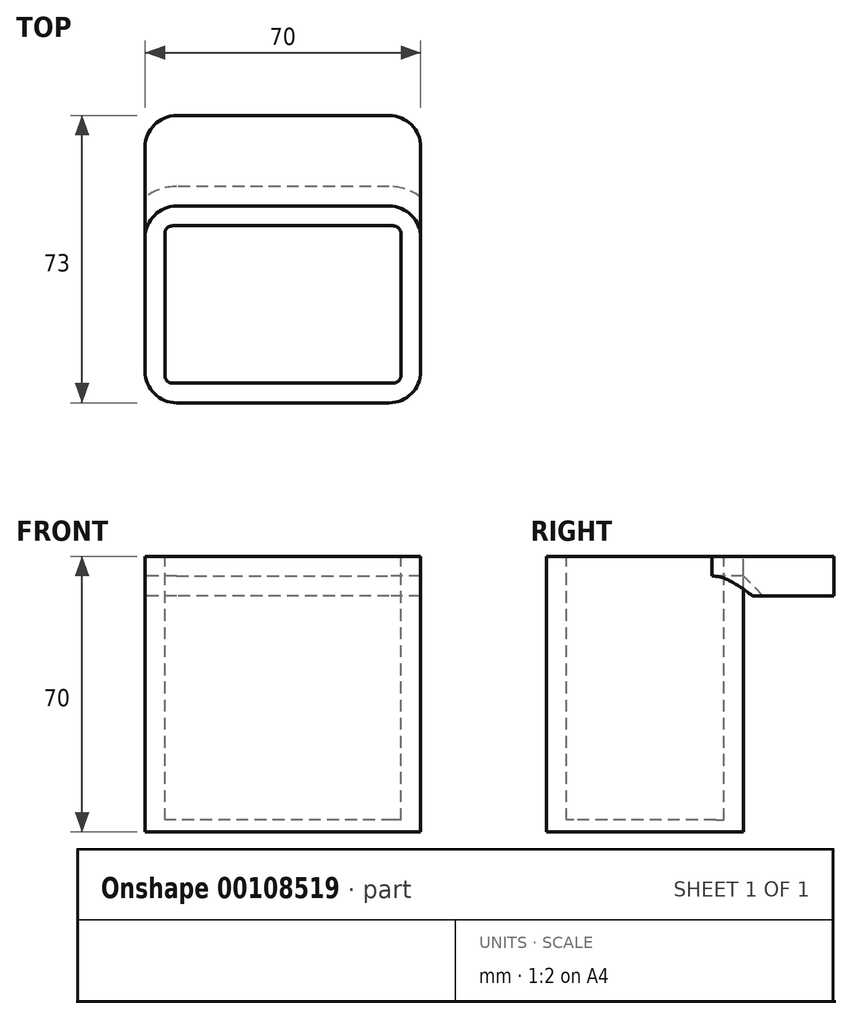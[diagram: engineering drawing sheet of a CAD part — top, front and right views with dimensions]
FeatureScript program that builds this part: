
annotation { "Feature Type Name" : "Feature", "Feature Type Description" : "" }
export const myFeature = defineFeature(function(context is Context, id is Id, definition is map)
    precondition{}
    {
        {
            var Q0;
            Q0=qCreatedBy(makeId("Top.planeOp"),FACE);
            var sketch = newSketch(context, id + "F0", { "sketchPlane" : qUnion([Q0])});
            skLineSegment(sketch, "E0.bottom", {"start": v(27, -25) * mm, "end": v(-27, -25) * mm});
            skLineSegment(sketch, "E0.top", {"start": v(27, 48) * mm, "end": v(-27, 48) * mm});
            skLineSegment(sketch, "E0.left", {"start": v(35, -17) * mm, "end": v(35, 17) * mm});
            skLineSegment(sketch, "E0.right", {"start": v(-35, -17) * mm, "end": v(-35, 17) * mm});
            skPoint(sketch, "E0.middle", {"position": v(0, 11.5) * mm});
            skLineSegment(sketch, "E1.bottom", {"start": v(28, 20) * mm, "end": v(-28, 20) * mm});
            skLineSegment(sketch, "E1.top", {"start": v(28, -20) * mm, "end": v(-28, -20) * mm});
            skLineSegment(sketch, "E1.left", {"start": v(30, 18) * mm, "end": v(30, -18) * mm});
            skLineSegment(sketch, "E1.right", {"start": v(-30, 18) * mm, "end": v(-30, -18) * mm});
            skPoint(sketch, "E1.middle", {"position": v(0, 0) * mm});
            skPoint(sketch, "E2", {"position": v(0, 20) * mm});
            skPoint(sketch, "E3.visualSharp", {"position": v(-30, 20) * mm});
            skArc(sketch, "E3.filletArc", {"start": v(-28, 20) * mm, "mid": v(-29.41, 19.41) * mm, "end": v(-30, 18) * mm});
            skPoint(sketch, "E4.visualSharp", {"position": v(30, 20) * mm});
            skArc(sketch, "E4.filletArc", {"start": v(30, 18) * mm, "mid": v(29.41, 19.41) * mm, "end": v(28, 20) * mm});
            skPoint(sketch, "E5.visualSharp", {"position": v(30, -20) * mm});
            skArc(sketch, "E5.filletArc", {"start": v(28, -20) * mm, "mid": v(29.41, -19.41) * mm, "end": v(30, -18) * mm});
            skPoint(sketch, "E6.visualSharp", {"position": v(-30, -20) * mm});
            skArc(sketch, "E6.filletArc", {"start": v(-30, -18) * mm, "mid": v(-29.41, -19.41) * mm, "end": v(-28, -20) * mm});
            skPoint(sketch, "E7.visualSharp", {"position": v(-35, 48) * mm});
            skArc(sketch, "E7.filletArc", {"start": v(-27, 48) * mm, "mid": v(-32.66, 45.66) * mm, "end": v(-35, 40) * mm});
            skPoint(sketch, "E8.visualSharp", {"position": v(35, 48) * mm});
            skArc(sketch, "E8.filletArc", {"start": v(35, 40) * mm, "mid": v(32.66, 45.66) * mm, "end": v(27, 48) * mm});
            skPoint(sketch, "E9.visualSharp", {"position": v(35, -25) * mm});
            skArc(sketch, "E9.filletArc", {"start": v(27, -25) * mm, "mid": v(32.66, -22.66) * mm, "end": v(35, -17) * mm});
            skPoint(sketch, "E10.visualSharp", {"position": v(-35, -25) * mm});
            skArc(sketch, "E10.filletArc", {"start": v(-35, -17) * mm, "mid": v(-32.66, -22.66) * mm, "end": v(-27, -25) * mm});
            skLineSegment(sketch, "E11", {"start": v(-27, 25) * mm, "end": v(27, 25) * mm});
            skArc(sketch, "E12.filletArc", {"start": v(-27, 25) * mm, "mid": v(-32.66, 22.66) * mm, "end": v(-35, 17) * mm});
            skArc(sketch, "E13.filletArc", {"start": v(35, 17) * mm, "mid": v(32.66, 22.66) * mm, "end": v(27, 25) * mm});
            skLineSegment(sketch, "E14", {"start": v(-35, 40) * mm, "end": v(-35, 17) * mm});
            skLineSegment(sketch, "E15", {"start": v(35, 40) * mm, "end": v(35, 17) * mm});
            skSolve(sketch);
        }
        {
            var Q0;
            Q0=makeQuery(id+"F0.imprint","IMPRINT",FACE,{"disambiguationData":[TD([[makeQuery(id+"F0.imprint","IMPRINT",EDGE,{"derivedFrom":sQuery(id+"F0.wireOp",EDGE,"E0.bottom")}),-1.0]])]});
            var Q1;
            Q1=makeQuery(id+"F0.imprint","IMPRINT",FACE,{"disambiguationData":[TD([[makeQuery(id+"F0.imprint","IMPRINT",EDGE,{"derivedFrom":sQuery(id+"F0.wireOp",EDGE,"E1.bottom")}),1.0]])]});
            extrude(context, id + "F1", {"entities" : qUnion([Q0, Q1]), "oppositeDirection" : true, "depth" : 70 * mm});
        }
        {
            var Q0;
            Q0=makeQuery(id+"F0.imprint","IMPRINT",FACE,{"disambiguationData":[TD([[makeQuery(id+"F0.imprint","IMPRINT",EDGE,{"derivedFrom":sQuery(id+"F0.wireOp",EDGE,"E1.bottom")}),1.0]])]});
            extrude(context, id + "F2", {"entities" : qUnion([Q0]), "operationType" : NewBodyOperationType.REMOVE, "oppositeDirection" : true, "depth" : 67 * mm});
        }
        {
            var Q0;
            Q0=makeQuery(id+"F0.imprint","IMPRINT",FACE,{"disambiguationData":[TD([[makeQuery(id+"F0.imprint","IMPRINT",EDGE,{"derivedFrom":sQuery(id+"F0.wireOp",EDGE,"E0.top")}),1.0]])]});
            extrude(context, id + "F3", {"entities" : qUnion([Q0]), "oppositeDirection" : true, "depth" : 10 * mm});
        }
        {
            var Q0;
            Q0=makeQuery(id+"F3.opExtrude","CAP_EDGE",EDGE,{"disambiguationData":[OSD([sQuery(id+"F0.wireOp",EDGE,"E11")])],"isStart":false});
            var Q1;
            Q1=makeQuery(id+"F3.opExtrude","CAP_EDGE",EDGE,{"disambiguationData":[OSD([sQuery(id+"F0.wireOp",EDGE,"E13.filletArc")])],"isStart":false});
            chamfer(context, id + "F4", {"entities" : qUnion([Q0, Q1]), "width" : 5 * mm, "tangentPropagation" : true});
        }
    });
